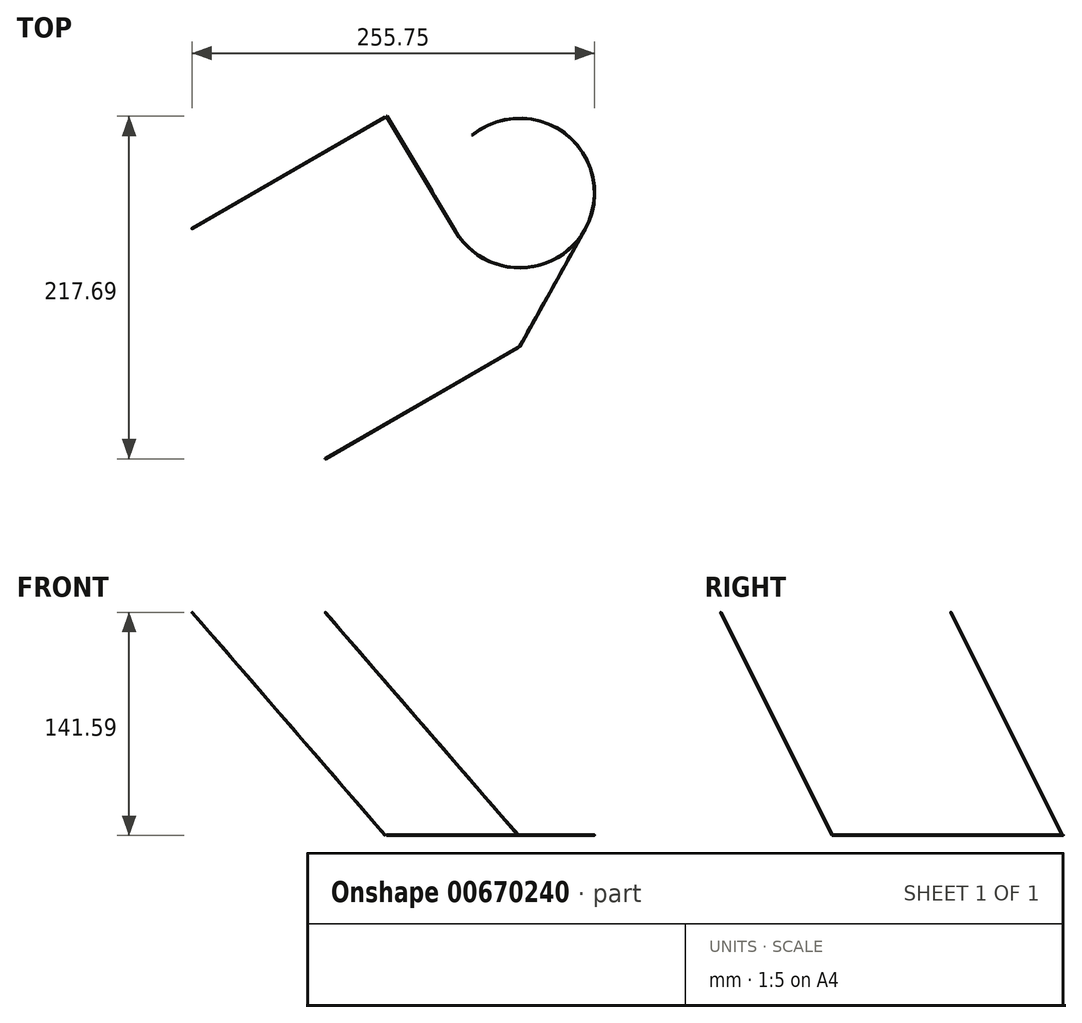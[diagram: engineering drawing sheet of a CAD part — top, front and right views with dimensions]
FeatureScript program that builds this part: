
annotation { "Feature Type Name" : "Feature", "Feature Type Description" : "" }
export const myFeature = defineFeature(function(context is Context, id is Id, definition is map)
    precondition{}
    {
        {
            var Q0;
            Q0=qCreatedBy(makeId("Front.planeOp"),FACE);
            var sketch = newSketch(context, id + "F0", { "sketchPlane" : qUnion([Q0])});
            skLineSegment(sketch, "E0", {"start": v(0, 0) * mm, "end": v(0, 36.12) * mm});
            skSolve(sketch);
        }
        {
            var Q0;
            Q0=qCreatedBy(makeId("Top.planeOp"),FACE);
            var sketch = newSketch(context, id + "F1", { "sketchPlane" : qUnion([Q0])});
            skCircle(sketch, "E1", {"center": v(0, 0) * mm, "radius": 47.5 * mm, "construction": true});
            skLineSegment(sketch, "E2", {"start": v(0, -97.5) * mm, "end": v(41.48, -23.14) * mm});
            skArc(sketch, "E3", {"start": v(41.48, -23.14) * mm, "mid": v(30.47, 36.44) * mm, "end": v(-30.12, 36.73) * mm});
            skCircle(sketch, "E4", {"center": v(0, 0) * mm, "radius": 97.5 * mm, "construction": true});
            skLineSegment(sketch, "E5", {"start": v(0, 0) * mm, "end": v(-84.44, 48.75) * mm, "construction": true});
            skLineSegment(sketch, "E6", {"start": v(-84.44, 48.75) * mm, "end": v(-40.78, -24.35) * mm});
            skArc(sketch, "E7", {"start": v(-40.78, -24.35) * mm, "mid": v(0.7, -47.5) * mm, "end": v(41.48, -23.14) * mm});
            skLineSegment(sketch, "E8", {"start": v(0, 0) * mm, "end": v(-23.75, 41.14) * mm, "construction": true});
            skSolve(sketch);
        }
        {
            var Q0;
            Q0=sQuery(id+"F1.wireOp",VERTEX,"E6.start");
            var Q1;
            Q1=sQuery(id+"F1.wireOp",EDGE,"E8");
            cPlane(context, id + "F2", {"entities" : qUnion([Q0, Q1]), "cplaneType" : CPlaneType.LINE_POINT, "offset" : 25 * mm, "width" : 150 * mm, "height" : 150 * mm});
        }
        {
            var Q0;
            Q0=sQuery(id+"F1.wireOp",VERTEX,"E2.start");
            var Q1;
            Q1=sQuery(id+"F1.wireOp",EDGE,"E8");
            cPlane(context, id + "F3", {"entities" : qUnion([Q0, Q1]), "cplaneType" : CPlaneType.LINE_POINT, "offset" : 25 * mm, "width" : 150 * mm, "height" : 150 * mm});
        }
        {
            var Q0;
            Q0=qCreatedBy(id+"F3.planeOp",FACE);
            var sketch = newSketch(context, id + "F4", { "sketchPlane" : qUnion([Q0])});
            skPoint(sketch, "E9", {"position": v(49.92, 0) * mm});
            skLineSegment(sketch, "E10", {"start": v(49.92, 0) * mm, "end": v(191.34, 141.42) * mm});
            skSolve(sketch);
        }
        {
            var Q0;
            Q0=qCreatedBy(id+"F2.planeOp",FACE);
            var sketch = newSketch(context, id + "F5", { "sketchPlane" : qUnion([Q0])});
            skLineSegment(sketch, "E11", {"start": v(50.08, 0) * mm, "end": v(191.5, 141.42) * mm});
            skSolve(sketch);
        }
        {
            var Q0;
            Q0=sQuery(id+"F4.wireOp",VERTEX,"E10.end");
            var Q1;
            Q1=sQuery(id+"F4.wireOp",EDGE,"E10");
            cPlane(context, id + "F6", {"entities" : qUnion([Q0, Q1]), "cplaneType" : CPlaneType.LINE_POINT, "offset" : 25 * mm, "width" : 150 * mm, "height" : 150 * mm});
        }
        {
            var Q0;
            Q0=sQuery(id+"F5.wireOp",VERTEX,"E11.end");
            var Q1;
            Q1=sQuery(id+"F5.wireOp",EDGE,"E11");
            cPlane(context, id + "F7", {"entities" : qUnion([Q0, Q1]), "cplaneType" : CPlaneType.LINE_POINT, "offset" : 25 * mm, "width" : 150 * mm, "height" : 150 * mm});
        }
        {
            var Q0;
            Q0=qCreatedBy(id+"F7.planeOp",FACE);
            var sketch = newSketch(context, id + "F8", { "sketchPlane" : qUnion([Q0])});
            skCircle(sketch, "E12", {"center": v(-80.84, 43) * mm, "radius": 0.1 * mm});
            skSolve(sketch);
        }
        {
            var Q0;
            Q0=qCreatedBy(id+"F6.planeOp",FACE);
            var sketch = newSketch(context, id + "F9", { "sketchPlane" : qUnion([Q0])});
            skCircle(sketch, "E13", {"center": v(26.06, -87.73) * mm, "radius": 0.1 * mm});
            skSolve(sketch);
        }
        {
            var Q0;
            Q0=makeQuery(id+"F9.imprint","IMPRINT",FACE,{"disambiguationData":[TD([[makeQuery(id+"F9.imprint","IMPRINT",EDGE,{"derivedFrom":sQuery(id+"F9.wireOp",EDGE,"E13")}),1.0]])]});
            var Q1;
            Q1=sQuery(id+"F4.wireOp",EDGE,"E10");
            sweep(context, id + "F10", {"profiles" : qUnion([Q0]), "path" : qUnion([Q1])});
        }
        {
            var Q0;
            Q0=makeQuery(id+"F8.imprint","IMPRINT",FACE,{"disambiguationData":[TD([[makeQuery(id+"F8.imprint","IMPRINT",EDGE,{"derivedFrom":sQuery(id+"F8.wireOp",EDGE,"E12")}),1.0]])]});
            var Q1;
            Q1=sQuery(id+"F5.wireOp",EDGE,"E11");
            sweep(context, id + "F11", {"profiles" : qUnion([Q0]), "path" : qUnion([Q1])});
        }
        {
            var Q0;
            Q0=sQuery(id+"F1.wireOp",VERTEX,"E7.start");
            var Q1;
            Q1=sQuery(id+"F1.wireOp",EDGE,"E6");
            cPlane(context, id + "F12", {"entities" : qUnion([Q0, Q1]), "cplaneType" : CPlaneType.LINE_POINT, "offset" : 25 * mm, "width" : 150 * mm, "height" : 150 * mm});
        }
        {
            var Q0;
            Q0=qCreatedBy(id+"F12.planeOp",FACE);
            var sketch = newSketch(context, id + "F13", { "sketchPlane" : qUnion([Q0])});
            skCircle(sketch, "E14", {"center": v(-47.5, 0) * mm, "radius": 0.1 * mm});
            skSolve(sketch);
        }
        {
            var Q0;
            Q0 = qSketchRegion(id + "F13", true);
            var Q1;
            Q1=sQuery(id+"F1.wireOp",EDGE,"E6");
            var Q2;
            Q2=sQuery(id+"F1.wireOp",EDGE,"E7");
            sweep(context, id + "F14", {"operationType" : NewBodyOperationType.ADD, "profiles" : qUnion([Q0]), "path" : qUnion([Q1, Q2])});
        }
        {
            var Q0;
            Q0=sQuery(id+"F1.wireOp",VERTEX,"E7.end");
            var Q1;
            Q1=sQuery(id+"F1.wireOp",EDGE,"E2");
            cPlane(context, id + "F15", {"entities" : qUnion([Q0, Q1]), "cplaneType" : CPlaneType.LINE_POINT, "offset" : 25 * mm, "width" : 150 * mm, "height" : 150 * mm});
        }
        {
            var Q0;
            Q0=qCreatedBy(id+"F15.planeOp",FACE);
            var sketch = newSketch(context, id + "F16", { "sketchPlane" : qUnion([Q0])});
            skCircle(sketch, "E15", {"center": v(-47.5, 0) * mm, "radius": 0.1 * mm});
            skSolve(sketch);
        }
        {
            var Q0;
            Q0 = qSketchRegion(id + "F16", true);
            var Q1;
            Q1=sQuery(id+"F1.wireOp",EDGE,"E2");
            var Q2;
            Q2=sQuery(id+"F1.wireOp",EDGE,"E3");
            sweep(context, id + "F17", {"profiles" : qUnion([Q0]), "path" : qUnion([Q1, Q2])});
        }
    });
